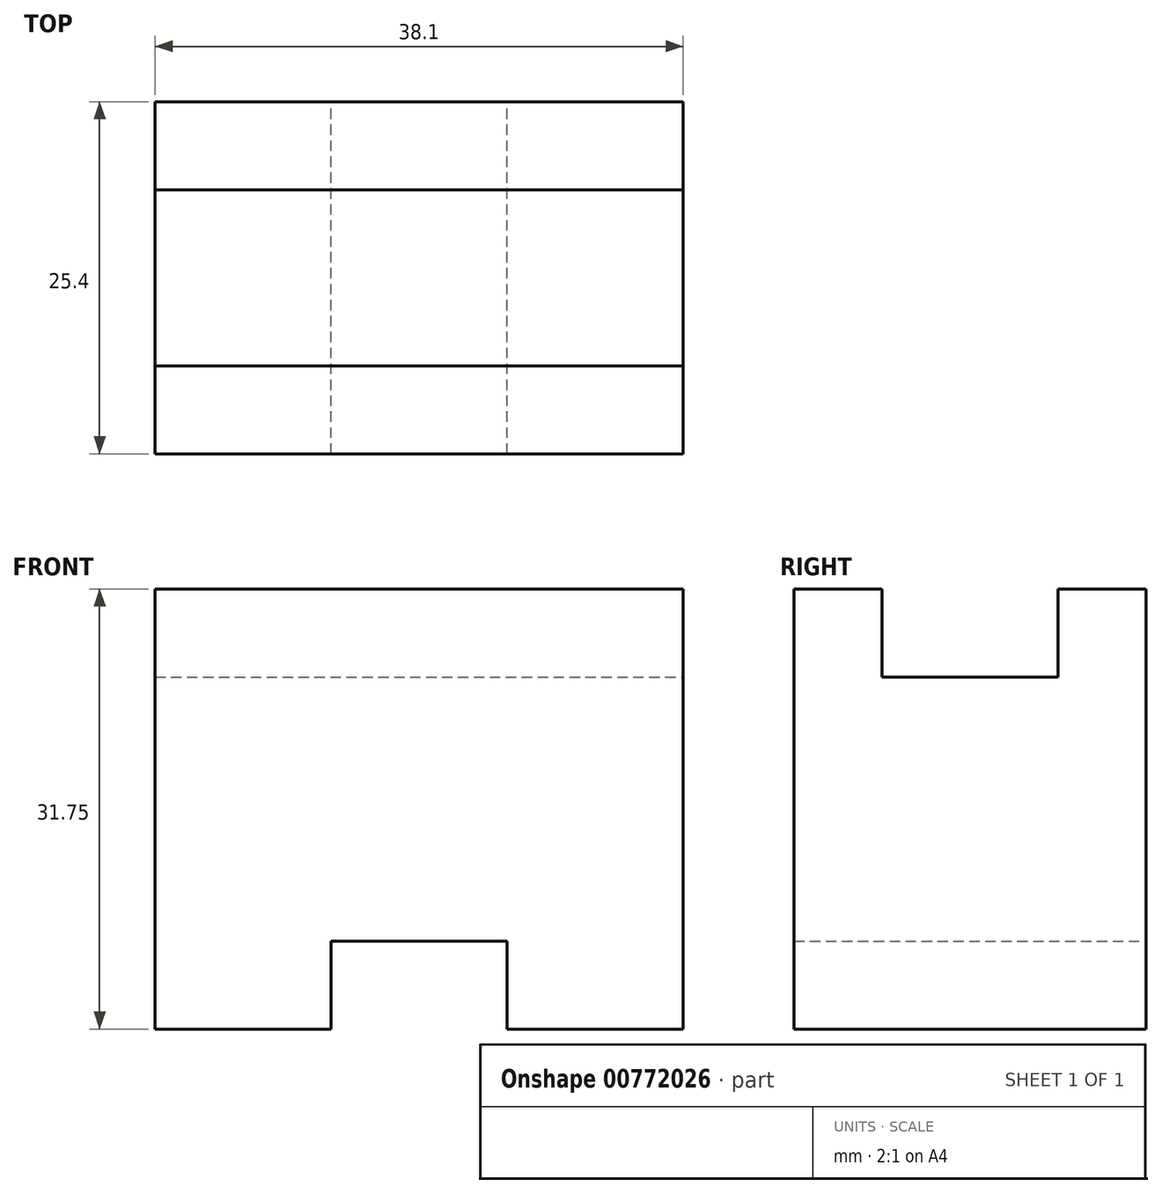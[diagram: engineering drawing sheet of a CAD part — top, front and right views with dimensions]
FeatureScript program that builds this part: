
annotation { "Feature Type Name" : "Feature", "Feature Type Description" : "" }
export const myFeature = defineFeature(function(context is Context, id is Id, definition is map)
    precondition{}
    {
        {
            var Q0;
            Q0=qCreatedBy(makeId("Front.planeOp"),FACE);
            var sketch = newSketch(context, id + "F0", { "sketchPlane" : qUnion([Q0])});
            skLineSegment(sketch, "E0", {"start": v(0, 0) * mm, "end": v(12.7, 0) * mm});
            skLineSegment(sketch, "E1", {"start": v(12.7, 0) * mm, "end": v(12.7, 6.35) * mm});
            skLineSegment(sketch, "E2", {"start": v(12.7, 6.35) * mm, "end": v(25.4, 6.35) * mm});
            skLineSegment(sketch, "E3", {"start": v(25.4, 6.35) * mm, "end": v(25.4, 0) * mm});
            skLineSegment(sketch, "E4", {"start": v(25.4, 0) * mm, "end": v(38.1, 0) * mm});
            skLineSegment(sketch, "E5", {"start": v(38.1, 0) * mm, "end": v(38.1, 31.75) * mm});
            skLineSegment(sketch, "E6", {"start": v(38.1, 31.75) * mm, "end": v(0, 31.75) * mm});
            skLineSegment(sketch, "E7", {"start": v(0, 31.75) * mm, "end": v(0, 0) * mm});
            skSolve(sketch);
        }
        {
            var Q0;
            Q0 = qSketchRegion(id + "F0", true);
            extrude(context, id + "F1", {"entities" : qUnion([Q0]), "depth" : 25.4 * mm, "offsetDistance" : 25.4 * mm});
        }
        {
            var Q0;
            Q0=makeQuery(id+"F1.opExtrude","SWEPT_FACE",FACE,{"disambiguationData":[OSD([sQuery(id+"F0.wireOp",EDGE,"E5")])]});
            var sketch = newSketch(context, id + "F2", { "sketchPlane" : qUnion([Q0])});
            skLineSegment(sketch, "E8", {"start": v(-25.4, 31.75) * mm, "end": v(-19.05, 31.75) * mm});
            skLineSegment(sketch, "E9", {"start": v(-19.05, 31.75) * mm, "end": v(-19.05, 25.4) * mm});
            skLineSegment(sketch, "E10", {"start": v(-19.05, 25.4) * mm, "end": v(-6.35, 25.4) * mm});
            skLineSegment(sketch, "E11", {"start": v(-6.35, 25.4) * mm, "end": v(-6.35, 31.75) * mm});
            skLineSegment(sketch, "E12", {"start": v(-6.35, 31.75) * mm, "end": v(0, 31.75) * mm});
            skSolve(sketch);
        }
        {
            var Q0;
            {var subQ0=sQuery(id+"F2.wireOp",EDGE,"E9");Q0=makeQuery(id+"F2.imprint","IMPRINT",FACE,{"disambiguationData":[TD([[makeQuery(id+"F2.imprint","IMPRINT",EDGE,{"derivedFrom":subQ0}),1.0]])]});}
            extrude(context, id + "F3", {"entities" : qUnion([Q0]), "operationType" : NewBodyOperationType.REMOVE, "oppositeDirection" : true, "depth" : 38.1 * mm, "offsetDistance" : 25.4 * mm});
        }
    });
